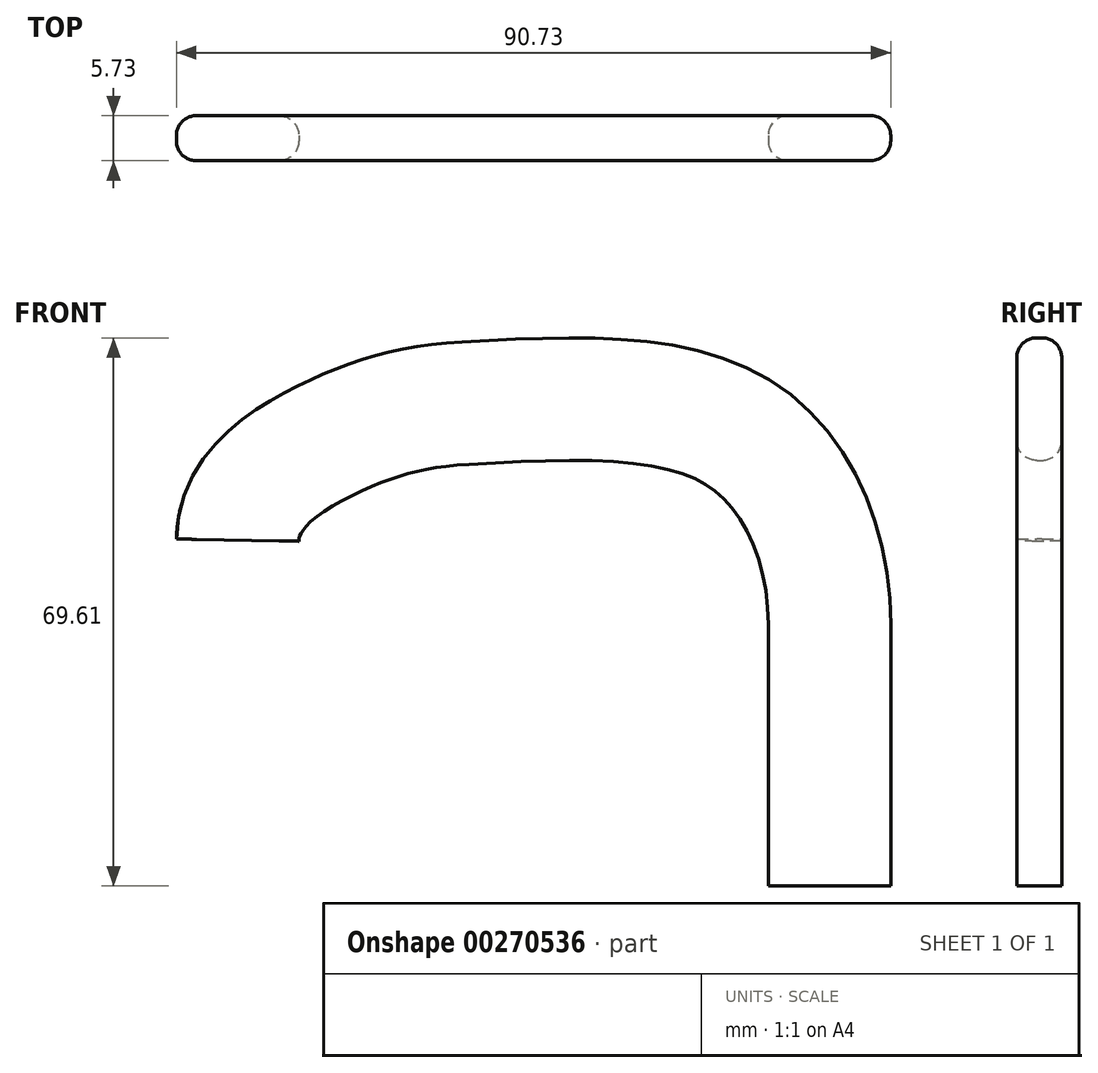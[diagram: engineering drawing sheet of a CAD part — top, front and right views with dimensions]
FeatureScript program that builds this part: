
annotation { "Feature Type Name" : "Feature", "Feature Type Description" : "" }
export const myFeature = defineFeature(function(context is Context, id is Id, definition is map)
    precondition{}
    {
        {
            var Q0;
            Q0=qCreatedBy(makeId("Top.planeOp"),FACE);
            var sketch = newSketch(context, id + "F0", { "sketchPlane" : qUnion([Q0])});
            skLineSegment(sketch, "E0.bottom", {"start": v(-6.14, 0.48) * mm, "end": v(4.33, 0.48) * mm});
            skLineSegment(sketch, "E0.top", {"start": v(-6.14, -5.25) * mm, "end": v(4.33, -5.25) * mm});
            skLineSegment(sketch, "E0.left", {"start": v(-8.68, -2.06) * mm, "end": v(-8.68, -2.7) * mm});
            skLineSegment(sketch, "E0.right", {"start": v(6.87, -2.06) * mm, "end": v(6.87, -2.7) * mm});
            skPoint(sketch, "E1.visualSharp", {"position": v(-8.68, 0.48) * mm});
            skArc(sketch, "E1.filletArc", {"start": v(-6.14, 0.48) * mm, "mid": v(-7.94, -0.26) * mm, "end": v(-8.68, -2.06) * mm});
            skPoint(sketch, "E2.visualSharp", {"position": v(6.87, -5.25) * mm});
            skArc(sketch, "E2.filletArc", {"start": v(4.33, -5.25) * mm, "mid": v(6.13, -4.5) * mm, "end": v(6.87, -2.7) * mm});
            skPoint(sketch, "E3.visualSharp", {"position": v(6.87, 0.48) * mm});
            skArc(sketch, "E3.filletArc", {"start": v(6.87, -2.06) * mm, "mid": v(6.13, -0.26) * mm, "end": v(4.33, 0.48) * mm});
            skPoint(sketch, "E4.visualSharp", {"position": v(-8.68, -5.25) * mm});
            skArc(sketch, "E4.filletArc", {"start": v(-8.68, -2.7) * mm, "mid": v(-7.94, -4.5) * mm, "end": v(-6.14, -5.25) * mm});
            skSolve(sketch);
        }
        {
            var Q0;
            Q0=qCreatedBy(makeId("Front.planeOp"),FACE);
            var sketch = newSketch(context, id + "F1", { "sketchPlane" : qUnion([Q0])});
            skLineSegment(sketch, "E5", {"start": v(0, 0) * mm, "end": v(0, 33.18) * mm});
            skFitSpline(sketch, "E6", {"points": [v(0, 33.18) * mm, v(-11.58, 58.07) * mm, v(-47.18, 62.22) * mm], "startDerivative": vector(0, 65.7) * mm, "endDerivative": vector(-77.94, -4.37) * mm});
            skFitSpline(sketch, "E7", {"points": [v(-47.18, 62.22) * mm, v(-64.55, 57.77) * mm, v(-77, 43.94) * mm], "startDerivative": vector(-41.58, -2.35) * mm, "endDerivative": vector(-0.78, -41.79) * mm});
            skSolve(sketch);
        }
        {
            var Q0;
            Q0=makeQuery(id+"F0.imprint","IMPRINT",FACE,{"disambiguationData":[TD([[makeQuery(id+"F0.imprint","IMPRINT",EDGE,{"derivedFrom":sQuery(id+"F0.wireOp",EDGE,"E0.bottom")}),-1.0]])]});
            var Q1;
            Q1=sQuery(id+"F1.wireOp",EDGE,"E5");
            var Q2;
            Q2=sQuery(id+"F1.wireOp",EDGE,"E6");
            var Q3;
            Q3=sQuery(id+"F1.wireOp",EDGE,"E7");
            sweep(context, id + "F2", {"profiles" : qUnion([Q0]), "path" : qUnion([Q1, Q2, Q3])});
        }
    });
